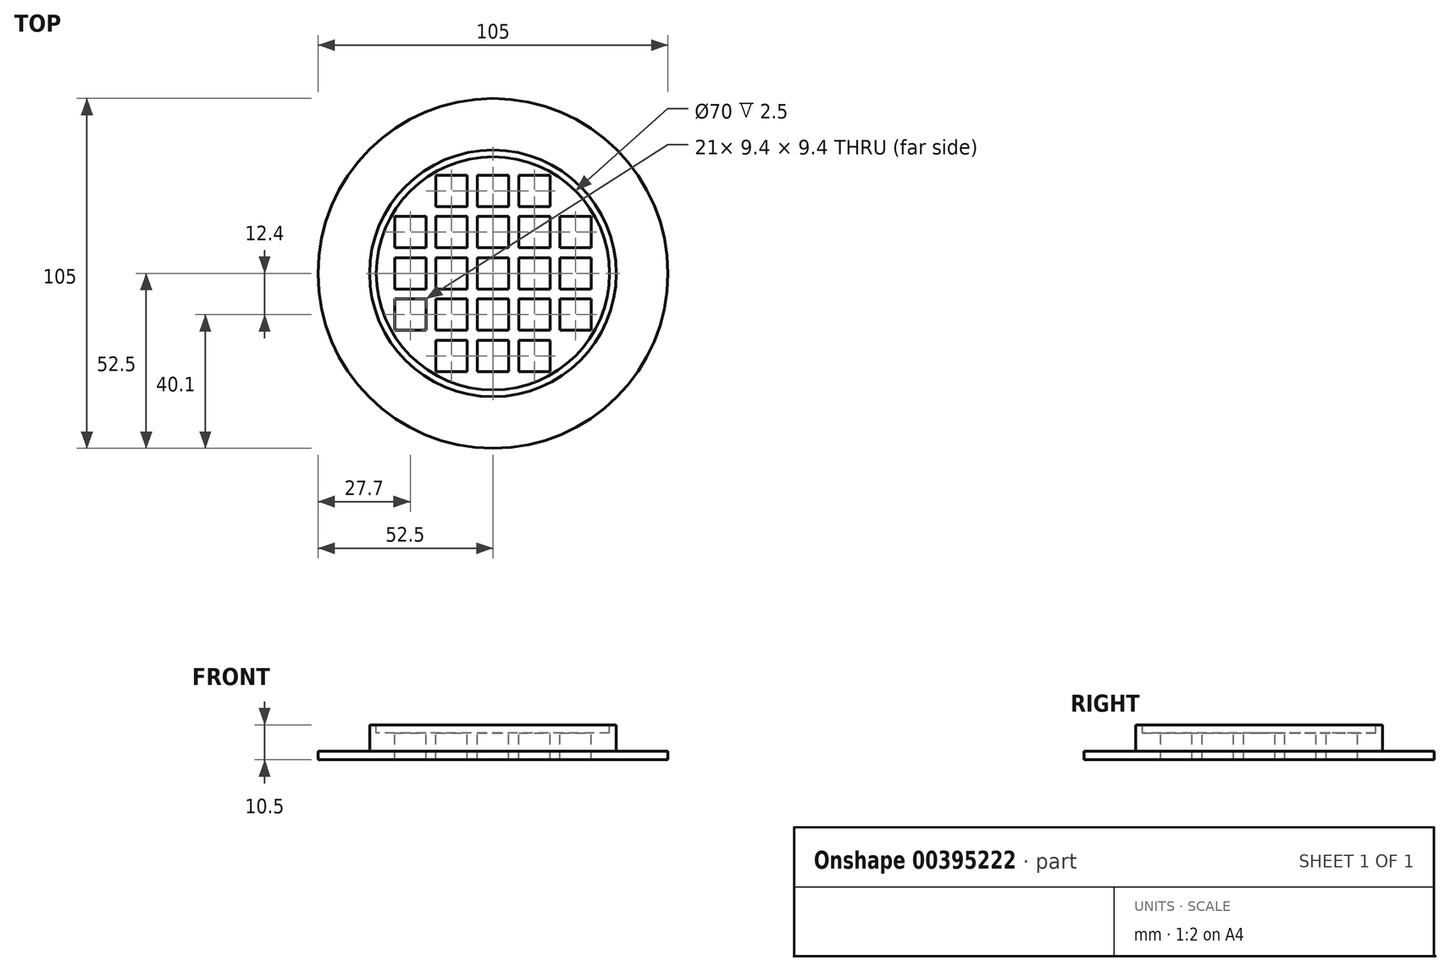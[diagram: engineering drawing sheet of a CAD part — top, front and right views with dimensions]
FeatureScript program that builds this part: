
annotation { "Feature Type Name" : "Feature", "Feature Type Description" : "" }
export const myFeature = defineFeature(function(context is Context, id is Id, definition is map)
    precondition{}
    {
        {
            var Q0;
            Q0=qCreatedBy(makeId("Front.planeOp"),FACE);
            var sketch = newSketch(context, id + "F0", { "sketchPlane" : qUnion([Q0])});
            skLineSegment(sketch, "E0.bottom", {"start": v(0, 0) * mm, "end": v(37, 0) * mm});
            skLineSegment(sketch, "E0.top", {"start": v(35, 10.5) * mm, "end": v(37, 10.5) * mm});
            skLineSegment(sketch, "E0.left", {"start": v(0, 0) * mm, "end": v(0, 8) * mm});
            skLineSegment(sketch, "E0.right", {"start": v(37, 2.6) * mm, "end": v(37, 10.5) * mm});
            skLineSegment(sketch, "E1.bottom", {"start": v(37, 2.6) * mm, "end": v(52.5, 2.6) * mm});
            skLineSegment(sketch, "E1.top", {"start": v(0, 0) * mm, "end": v(52.5, 0) * mm});
            skLineSegment(sketch, "E1.left", {"start": v(0, 2.6) * mm, "end": v(0, 0) * mm});
            skLineSegment(sketch, "E1.right", {"start": v(52.5, 2.6) * mm, "end": v(52.5, 0) * mm});
            skLineSegment(sketch, "E2.top", {"start": v(0, 8) * mm, "end": v(35, 8) * mm});
            skLineSegment(sketch, "E2.right", {"start": v(35, 10.5) * mm, "end": v(35, 8) * mm});
            skLineSegment(sketch, "E3", {"start": v(0, 58.56) * mm, "end": v(0, -53.85) * mm, "construction": true});
            skSolve(sketch);
        }
        {
            var Q0;
            Q0=makeQuery(id+"F0.imprint","IMPRINT",FACE,{"disambiguationData":[TD([[makeQuery(id+"F0.imprint","IMPRINT",EDGE,{"derivedFrom":sQuery(id+"F0.wireOp",EDGE,"E0.top")}),-1.0]])]});
            var Q1;
            Q1=sQuery(id+"F0.wireOp",EDGE,"E3");
            revolve(context, id + "F1", {"entities" : qUnion([Q0]), "axis" : qUnion([Q1]), "revolveType" : RevolveType.FULL});
        }
        {
            var Q0;
            Q0=makeQuery(id+"F1.opRevolve","SWEPT_FACE",FACE,{"disambiguationData":[OSD([sQuery(id+"F0.wireOp",EDGE,"E2.top")])]});
            var sketch = newSketch(context, id + "F2", { "sketchPlane" : qUnion([Q0])});
            skLineSegment(sketch, "E4.bottom", {"start": v(-4.7, 4.7) * mm, "end": v(4.7, 4.7) * mm});
            skLineSegment(sketch, "E4.top", {"start": v(-4.7, -4.7) * mm, "end": v(4.7, -4.7) * mm});
            skLineSegment(sketch, "E4.left", {"start": v(-4.7, 4.7) * mm, "end": v(-4.7, -4.7) * mm});
            skLineSegment(sketch, "E4.right", {"start": v(4.7, 4.7) * mm, "end": v(4.7, -4.7) * mm});
            skPoint(sketch, "E4.middle", {"position": v(0, 0) * mm});
            skPoint(sketch, "E5.0.1.0", {"position": v(0, 12.4) * mm});
            skLineSegment(sketch, "E5.0.1.1", {"start": v(4.7, 17.1) * mm, "end": v(4.7, 7.7) * mm});
            skLineSegment(sketch, "E5.0.1.2", {"start": v(-4.7, 17.1) * mm, "end": v(-4.7, 7.7) * mm});
            skLineSegment(sketch, "E5.0.1.3", {"start": v(-4.7, 7.7) * mm, "end": v(4.7, 7.7) * mm});
            skLineSegment(sketch, "E5.0.1.4", {"start": v(-4.7, 17.1) * mm, "end": v(4.7, 17.1) * mm});
            skPoint(sketch, "E5.0.2.0", {"position": v(0, 24.8) * mm});
            skLineSegment(sketch, "E5.0.2.1", {"start": v(4.7, 29.5) * mm, "end": v(4.7, 20.1) * mm});
            skLineSegment(sketch, "E5.0.2.2", {"start": v(-4.7, 29.5) * mm, "end": v(-4.7, 20.1) * mm});
            skLineSegment(sketch, "E5.0.2.3", {"start": v(-4.7, 20.1) * mm, "end": v(4.7, 20.1) * mm});
            skLineSegment(sketch, "E5.0.2.4", {"start": v(-4.7, 29.5) * mm, "end": v(4.7, 29.5) * mm});
            skPoint(sketch, "E5.1.0.0", {"position": v(12.4, 0) * mm});
            skLineSegment(sketch, "E5.1.0.1", {"start": v(17.1, 4.7) * mm, "end": v(17.1, -4.7) * mm});
            skLineSegment(sketch, "E5.1.0.2", {"start": v(7.7, 4.7) * mm, "end": v(7.7, -4.7) * mm});
            skLineSegment(sketch, "E5.1.0.3", {"start": v(7.7, -4.7) * mm, "end": v(17.1, -4.7) * mm});
            skLineSegment(sketch, "E5.1.0.4", {"start": v(7.7, 4.7) * mm, "end": v(17.1, 4.7) * mm});
            skPoint(sketch, "E5.1.1.0", {"position": v(12.4, 12.4) * mm});
            skLineSegment(sketch, "E5.1.1.1", {"start": v(17.1, 17.1) * mm, "end": v(17.1, 7.7) * mm});
            skLineSegment(sketch, "E5.1.1.2", {"start": v(7.7, 17.1) * mm, "end": v(7.7, 7.7) * mm});
            skLineSegment(sketch, "E5.1.1.3", {"start": v(7.7, 7.7) * mm, "end": v(17.1, 7.7) * mm});
            skLineSegment(sketch, "E5.1.1.4", {"start": v(7.7, 17.1) * mm, "end": v(17.1, 17.1) * mm});
            skPoint(sketch, "E5.1.2.0", {"position": v(12.4, 24.8) * mm});
            skLineSegment(sketch, "E5.1.2.1", {"start": v(17.1, 29.5) * mm, "end": v(17.1, 20.1) * mm});
            skLineSegment(sketch, "E5.1.2.2", {"start": v(7.7, 29.5) * mm, "end": v(7.7, 20.1) * mm});
            skLineSegment(sketch, "E5.1.2.3", {"start": v(7.7, 20.1) * mm, "end": v(17.1, 20.1) * mm});
            skLineSegment(sketch, "E5.1.2.4", {"start": v(7.7, 29.5) * mm, "end": v(17.1, 29.5) * mm});
            skPoint(sketch, "E5.2.0.0", {"position": v(24.8, 0) * mm});
            skLineSegment(sketch, "E5.2.0.1", {"start": v(29.5, 4.7) * mm, "end": v(29.5, -4.7) * mm});
            skLineSegment(sketch, "E5.2.0.2", {"start": v(20.1, 4.7) * mm, "end": v(20.1, -4.7) * mm});
            skLineSegment(sketch, "E5.2.0.3", {"start": v(20.1, -4.7) * mm, "end": v(29.5, -4.7) * mm});
            skLineSegment(sketch, "E5.2.0.4", {"start": v(20.1, 4.7) * mm, "end": v(29.5, 4.7) * mm});
            skPoint(sketch, "E5.2.1.0", {"position": v(24.8, 12.4) * mm});
            skLineSegment(sketch, "E5.2.1.1", {"start": v(29.5, 17.1) * mm, "end": v(29.5, 7.7) * mm});
            skLineSegment(sketch, "E5.2.1.2", {"start": v(20.1, 17.1) * mm, "end": v(20.1, 7.7) * mm});
            skLineSegment(sketch, "E5.2.1.3", {"start": v(20.1, 7.7) * mm, "end": v(29.5, 7.7) * mm});
            skLineSegment(sketch, "E5.2.1.4", {"start": v(20.1, 17.1) * mm, "end": v(29.5, 17.1) * mm});
            skLineSegment(sketch, "E5.direction1", {"start": v(-4.7, -4.7) * mm, "end": v(7.7, -4.7) * mm, "construction": true});
            skLineSegment(sketch, "E5.direction2", {"start": v(-4.7, -4.7) * mm, "end": v(-4.7, 7.7) * mm, "construction": true});
            skLineSegment(sketch, "E6.1.0.0", {"start": v(-17.1, -4.7) * mm, "end": v(-17.1, 7.7) * mm, "construction": true});
            skPoint(sketch, "E6.1.0.1", {"position": v(-12.4, 24.8) * mm});
            skLineSegment(sketch, "E6.1.0.2", {"start": v(-17.1, 4.7) * mm, "end": v(-7.7, 4.7) * mm});
            skLineSegment(sketch, "E6.1.0.3", {"start": v(-17.1, -4.7) * mm, "end": v(-7.7, -4.7) * mm});
            skLineSegment(sketch, "E6.1.0.4", {"start": v(-7.7, 4.7) * mm, "end": v(-7.7, -4.7) * mm});
            skLineSegment(sketch, "E6.1.0.5", {"start": v(-7.7, 17.1) * mm, "end": v(-7.7, 7.7) * mm});
            skLineSegment(sketch, "E6.1.0.6", {"start": v(-17.1, 17.1) * mm, "end": v(-17.1, 7.7) * mm});
            skLineSegment(sketch, "E6.1.0.7", {"start": v(-17.1, 7.7) * mm, "end": v(-7.7, 7.7) * mm});
            skLineSegment(sketch, "E6.1.0.8", {"start": v(-17.1, 17.1) * mm, "end": v(-7.7, 17.1) * mm});
            skLineSegment(sketch, "E6.1.0.9", {"start": v(-7.7, 29.5) * mm, "end": v(-7.7, 20.1) * mm});
            skLineSegment(sketch, "E6.1.0.10", {"start": v(-17.1, 29.5) * mm, "end": v(-17.1, 20.1) * mm});
            skLineSegment(sketch, "E6.1.0.11", {"start": v(-17.1, 20.1) * mm, "end": v(-7.7, 20.1) * mm});
            skLineSegment(sketch, "E6.1.0.12", {"start": v(-17.1, 29.5) * mm, "end": v(-7.7, 29.5) * mm});
            skPoint(sketch, "E6.1.0.13", {"position": v(-12.4, 12.4) * mm});
            skPoint(sketch, "E6.1.0.14", {"position": v(-12.4, 0) * mm});
            skLineSegment(sketch, "E6.1.0.15", {"start": v(-17.1, 4.7) * mm, "end": v(-17.1, -4.7) * mm});
            skLineSegment(sketch, "E6.2.0.0", {"start": v(-29.5, -4.7) * mm, "end": v(-29.5, 7.7) * mm, "construction": true});
            skLineSegment(sketch, "E6.2.0.2", {"start": v(-29.5, 4.7) * mm, "end": v(-20.1, 4.7) * mm});
            skLineSegment(sketch, "E6.2.0.3", {"start": v(-29.5, -4.7) * mm, "end": v(-20.1, -4.7) * mm});
            skLineSegment(sketch, "E6.2.0.4", {"start": v(-20.1, 4.7) * mm, "end": v(-20.1, -4.7) * mm});
            skLineSegment(sketch, "E6.2.0.5", {"start": v(-20.1, 17.1) * mm, "end": v(-20.1, 7.7) * mm});
            skLineSegment(sketch, "E6.2.0.6", {"start": v(-29.5, 17.1) * mm, "end": v(-29.5, 7.7) * mm});
            skLineSegment(sketch, "E6.2.0.7", {"start": v(-29.5, 7.7) * mm, "end": v(-20.1, 7.7) * mm});
            skLineSegment(sketch, "E6.2.0.8", {"start": v(-29.5, 17.1) * mm, "end": v(-20.1, 17.1) * mm});
            skPoint(sketch, "E6.2.0.13", {"position": v(-24.8, 12.4) * mm});
            skPoint(sketch, "E6.2.0.14", {"position": v(-24.8, 0) * mm});
            skLineSegment(sketch, "E6.2.0.15", {"start": v(-29.5, 4.7) * mm, "end": v(-29.5, -4.7) * mm});
            skLineSegment(sketch, "E6.direction1", {"start": v(-4.7, -4.7) * mm, "end": v(-17.1, -4.7) * mm, "construction": true});
            skLineSegment(sketch, "E7", {"start": v(-64.6, 0) * mm, "end": v(66.22, 0) * mm, "construction": true});
            skLineSegment(sketch, "E8.MirrorCS", {"start": v(-29.5, -4.7) * mm, "end": v(-29.5, 4.7) * mm});
            skLineSegment(sketch, "E9.MirrorCS", {"start": v(-17.1, -17.1) * mm, "end": v(-7.7, -17.1) * mm});
            skLineSegment(sketch, "E10.MirrorCS", {"start": v(-17.1, -20.1) * mm, "end": v(-7.7, -20.1) * mm});
            skLineSegment(sketch, "E11.MirrorCS", {"start": v(-29.5, 4.7) * mm, "end": v(-29.5, -7.7) * mm, "construction": true});
            skLineSegment(sketch, "E12.MirrorCS", {"start": v(-17.1, -4.7) * mm, "end": v(-17.1, 4.7) * mm});
            skLineSegment(sketch, "E13.MirrorCS", {"start": v(-4.7, -4.7) * mm, "end": v(-4.7, 4.7) * mm});
            skLineSegment(sketch, "E14.MirrorCS", {"start": v(-7.7, -4.7) * mm, "end": v(-7.7, 4.7) * mm});
            skLineSegment(sketch, "E15.MirrorCS", {"start": v(-7.7, -17.1) * mm, "end": v(-7.7, -7.7) * mm});
            skLineSegment(sketch, "E16.MirrorCS", {"start": v(20.1, -17.1) * mm, "end": v(29.5, -17.1) * mm});
            skLineSegment(sketch, "E17.MirrorCS", {"start": v(20.1, -7.7) * mm, "end": v(29.5, -7.7) * mm});
            skLineSegment(sketch, "E18.MirrorCS", {"start": v(-29.5, -7.7) * mm, "end": v(-20.1, -7.7) * mm});
            skLineSegment(sketch, "E19.MirrorCS", {"start": v(29.5, -4.7) * mm, "end": v(29.5, 4.7) * mm});
            skLineSegment(sketch, "E20.MirrorCS", {"start": v(-4.7, -17.1) * mm, "end": v(-4.7, -7.7) * mm});
            skPoint(sketch, "E21.MirrorP", {"position": v(-12.4, -24.8) * mm});
            skLineSegment(sketch, "E22.MirrorCS", {"start": v(17.1, -4.7) * mm, "end": v(17.1, 4.7) * mm});
            skLineSegment(sketch, "E23.MirrorCS", {"start": v(7.7, -29.5) * mm, "end": v(7.7, -20.1) * mm});
            skLineSegment(sketch, "E24.MirrorCS", {"start": v(20.1, -4.7) * mm, "end": v(20.1, 4.7) * mm});
            skLineSegment(sketch, "E25.MirrorCS", {"start": v(-4.7, -7.7) * mm, "end": v(4.7, -7.7) * mm});
            skLineSegment(sketch, "E26.MirrorCS", {"start": v(-4.7, -17.1) * mm, "end": v(4.7, -17.1) * mm});
            skLineSegment(sketch, "E27.MirrorCS", {"start": v(29.5, -17.1) * mm, "end": v(29.5, -7.7) * mm});
            skLineSegment(sketch, "E28.MirrorCS", {"start": v(-17.1, -7.7) * mm, "end": v(-7.7, -7.7) * mm});
            skLineSegment(sketch, "E29.MirrorCS", {"start": v(-20.1, -4.7) * mm, "end": v(-20.1, 4.7) * mm});
            skLineSegment(sketch, "E30.MirrorCS", {"start": v(4.7, -29.5) * mm, "end": v(4.7, -20.1) * mm});
            skLineSegment(sketch, "E31.MirrorCS", {"start": v(7.7, -17.1) * mm, "end": v(7.7, -7.7) * mm});
            skLineSegment(sketch, "E32.MirrorCS", {"start": v(17.1, -17.1) * mm, "end": v(17.1, -7.7) * mm});
            skLineSegment(sketch, "E33.MirrorCS", {"start": v(-4.7, 4.7) * mm, "end": v(-4.7, -7.7) * mm, "construction": true});
            skLineSegment(sketch, "E34.MirrorCS", {"start": v(-29.5, -17.1) * mm, "end": v(-20.1, -17.1) * mm});
            skLineSegment(sketch, "E35.MirrorCS", {"start": v(-7.7, -29.5) * mm, "end": v(-7.7, -20.1) * mm});
            skLineSegment(sketch, "E36.MirrorCS", {"start": v(7.7, -17.1) * mm, "end": v(17.1, -17.1) * mm});
            skLineSegment(sketch, "E37.MirrorCS", {"start": v(-4.7, 4.7) * mm, "end": v(-17.1, 4.7) * mm, "construction": true});
            skLineSegment(sketch, "E38.MirrorCS", {"start": v(4.7, -17.1) * mm, "end": v(4.7, -7.7) * mm});
            skLineSegment(sketch, "E39.MirrorCS", {"start": v(7.7, -20.1) * mm, "end": v(17.1, -20.1) * mm});
            skLineSegment(sketch, "E40.MirrorCS", {"start": v(17.1, -29.5) * mm, "end": v(17.1, -20.1) * mm});
            skLineSegment(sketch, "E41.MirrorCS", {"start": v(-4.7, -29.5) * mm, "end": v(4.7, -29.5) * mm});
            skPoint(sketch, "E42.MirrorP", {"position": v(12.4, -24.8) * mm});
            skLineSegment(sketch, "E43.MirrorCS", {"start": v(-4.7, 4.7) * mm, "end": v(7.7, 4.7) * mm, "construction": true});
            skLineSegment(sketch, "E44.MirrorCS", {"start": v(7.7, -4.7) * mm, "end": v(7.7, 4.7) * mm});
            skPoint(sketch, "E45.MirrorP", {"position": v(-12.4, -12.4) * mm});
            skLineSegment(sketch, "E46.MirrorCS", {"start": v(-17.1, -29.5) * mm, "end": v(-7.7, -29.5) * mm});
            skLineSegment(sketch, "E47.MirrorCS", {"start": v(-17.1, -17.1) * mm, "end": v(-17.1, -7.7) * mm});
            skLineSegment(sketch, "E48.MirrorCS", {"start": v(4.7, -4.7) * mm, "end": v(4.7, 4.7) * mm});
            skPoint(sketch, "E49.MirrorP", {"position": v(24.8, -12.4) * mm});
            skLineSegment(sketch, "E50.MirrorCS", {"start": v(7.7, -29.5) * mm, "end": v(17.1, -29.5) * mm});
            skLineSegment(sketch, "E51.MirrorCS", {"start": v(-17.1, -29.5) * mm, "end": v(-17.1, -20.1) * mm});
            skPoint(sketch, "E52.MirrorP", {"position": v(0, -12.4) * mm});
            skLineSegment(sketch, "E53.MirrorCS", {"start": v(-4.7, -29.5) * mm, "end": v(-4.7, -20.1) * mm});
            skLineSegment(sketch, "E54.MirrorCS", {"start": v(-4.7, -20.1) * mm, "end": v(4.7, -20.1) * mm});
            skPoint(sketch, "E55.MirrorP", {"position": v(0, -24.8) * mm});
            skLineSegment(sketch, "E56.MirrorCS", {"start": v(-20.1, -17.1) * mm, "end": v(-20.1, -7.7) * mm});
            skLineSegment(sketch, "E57.MirrorCS", {"start": v(7.7, -7.7) * mm, "end": v(17.1, -7.7) * mm});
            skPoint(sketch, "E58.MirrorP", {"position": v(-24.8, -12.4) * mm});
            skLineSegment(sketch, "E59.MirrorCS", {"start": v(-29.5, -17.1) * mm, "end": v(-29.5, -7.7) * mm});
            skLineSegment(sketch, "E60.MirrorCS", {"start": v(-17.1, 4.7) * mm, "end": v(-17.1, -7.7) * mm, "construction": true});
            skLineSegment(sketch, "E61.MirrorCS", {"start": v(20.1, -17.1) * mm, "end": v(20.1, -7.7) * mm});
            skPoint(sketch, "E62.MirrorP", {"position": v(12.4, -12.4) * mm});
            skSolve(sketch);
        }
        {
            var Q0;
            Q0 = qSketchRegion(id + "F2", true);
            extrude(context, id + "F3", {"entities" : qUnion([Q0]), "operationType" : NewBodyOperationType.REMOVE, "oppositeDirection" : true, "depth" : 25 * mm});
        }
    });
